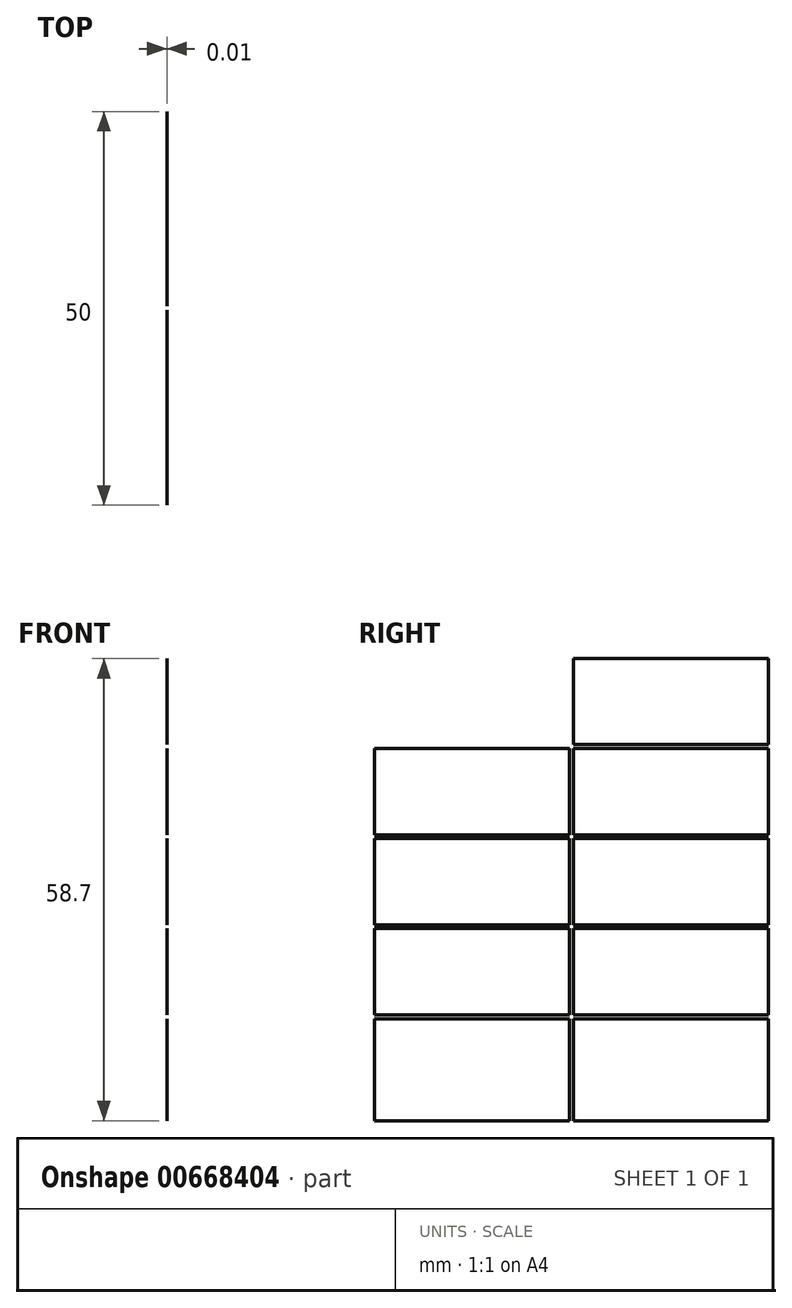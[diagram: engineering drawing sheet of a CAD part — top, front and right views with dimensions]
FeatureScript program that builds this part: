
annotation { "Feature Type Name" : "Feature", "Feature Type Description" : "" }
export const myFeature = defineFeature(function(context is Context, id is Id, definition is map)
    precondition{}
    {
        {
            var Q0;
            Q0=qCreatedBy(makeId("Right.planeOp"),FACE);
            var sketch = newSketch(context, id + "F0", { "sketchPlane" : qUnion([Q0])});
            skPoint(sketch, "E0.0", {"position": v(0, 0) * mm});
            skLineSegment(sketch, "E1.bottom", {"start": v(0, 0) * mm, "end": v(50, 0) * mm});
            skLineSegment(sketch, "E1.top", {"start": v(0, -60) * mm, "end": v(50, -60) * mm});
            skLineSegment(sketch, "E1.left", {"start": v(0, 0) * mm, "end": v(0, -12.24) * mm});
            skLineSegment(sketch, "E1.right", {"start": v(50, 0) * mm, "end": v(50, -12.24) * mm});
            skPoint(sketch, "E2.MirrorP", {"position": v(11.5, 0) * mm});
            skPoint(sketch, "E3.MirrorP", {"position": v(18.5, 0) * mm});
            skPoint(sketch, "E4.MirrorP", {"position": v(30, 0) * mm});
            skLineSegment(sketch, "E5.0", {"start": v(25.25, -60) * mm, "end": v(25.25, -52.76) * mm});
            skLineSegment(sketch, "E6.0", {"start": v(24.75, -60) * mm, "end": v(24.75, -52.76) * mm});
            skLineSegment(sketch, "E7.trimOffspring", {"start": v(25.25, -1.3) * mm, "end": v(50, -1.3) * mm});
            skLineSegment(sketch, "E8.0", {"start": v(0, -12.24) * mm, "end": v(24.75, -12.24) * mm});
            skLineSegment(sketch, "E9.0", {"start": v(0, -12.74) * mm, "end": v(24.75, -12.74) * mm});
            skLineSegment(sketch, "E10.trimOffspring", {"start": v(25.25, -6.52) * mm, "end": v(25.25, -1.3) * mm});
            skLineSegment(sketch, "E11.trimOffspring", {"start": v(25.25, -12.24) * mm, "end": v(50, -12.24) * mm});
            skLineSegment(sketch, "E12.trimOffspring", {"start": v(25.25, -12.24) * mm, "end": v(25.25, -7.02) * mm});
            skLineSegment(sketch, "E13.trimOffspring", {"start": v(25.25, -12.74) * mm, "end": v(50, -12.74) * mm});
            skLineSegment(sketch, "E14.trimOffspring", {"start": v(25.25, -17.95) * mm, "end": v(25.25, -12.74) * mm});
            skLineSegment(sketch, "E15.0", {"start": v(0, -23.67) * mm, "end": v(24.75, -23.67) * mm});
            skLineSegment(sketch, "E16.0", {"start": v(0, -24.17) * mm, "end": v(24.75, -24.17) * mm});
            skLineSegment(sketch, "E17.trimOffspring", {"start": v(25.25, -23.67) * mm, "end": v(50, -23.67) * mm});
            skLineSegment(sketch, "E18.trimOffspring", {"start": v(25.25, -23.67) * mm, "end": v(25.25, -18.45) * mm});
            skLineSegment(sketch, "E19.trimOffspring", {"start": v(25.25, -24.17) * mm, "end": v(50, -24.17) * mm});
            skLineSegment(sketch, "E20.trimOffspring", {"start": v(25.25, -29.39) * mm, "end": v(25.25, -24.17) * mm});
            skLineSegment(sketch, "E21.trimOffspring", {"start": v(24.75, -29.39) * mm, "end": v(24.75, -24.17) * mm});
            skLineSegment(sketch, "E22.0", {"start": v(0, -35.1) * mm, "end": v(24.75, -35.1) * mm});
            skLineSegment(sketch, "E23.0", {"start": v(0, -35.6) * mm, "end": v(24.75, -35.6) * mm});
            skLineSegment(sketch, "E24.trimOffspring", {"start": v(25.25, -35.1) * mm, "end": v(50, -35.1) * mm});
            skLineSegment(sketch, "E25.trimOffspring", {"start": v(25.25, -35.1) * mm, "end": v(25.25, -29.89) * mm});
            skLineSegment(sketch, "E26.trimOffspring", {"start": v(24.75, -35.1) * mm, "end": v(24.75, -29.89) * mm});
            skLineSegment(sketch, "E27.trimOffspring", {"start": v(25.25, -35.6) * mm, "end": v(50, -35.6) * mm});
            skLineSegment(sketch, "E28.trimOffspring", {"start": v(25.25, -40.82) * mm, "end": v(25.25, -35.6) * mm});
            skLineSegment(sketch, "E29.trimOffspring", {"start": v(24.75, -40.82) * mm, "end": v(24.75, -35.6) * mm});
            skLineSegment(sketch, "E30.0", {"start": v(0, -46.54) * mm, "end": v(24.75, -46.54) * mm});
            skLineSegment(sketch, "E31.0", {"start": v(0, -47.04) * mm, "end": v(24.75, -47.04) * mm});
            skLineSegment(sketch, "E32.trimOffspring", {"start": v(25.25, -46.54) * mm, "end": v(50, -46.54) * mm});
            skLineSegment(sketch, "E33.trimOffspring", {"start": v(25.25, -46.54) * mm, "end": v(25.25, -41.32) * mm});
            skLineSegment(sketch, "E34.trimOffspring", {"start": v(24.75, -46.54) * mm, "end": v(24.75, -41.32) * mm});
            skLineSegment(sketch, "E35.trimOffspring", {"start": v(25.25, -47.04) * mm, "end": v(50, -47.04) * mm});
            skLineSegment(sketch, "E36.trimOffspring", {"start": v(25.25, -52.26) * mm, "end": v(25.25, -47.04) * mm});
            skLineSegment(sketch, "E37.trimOffspring", {"start": v(24.75, -52.26) * mm, "end": v(24.75, -47.04) * mm});
            skLineSegment(sketch, "E38", {"start": v(25.25, -6.52) * mm, "end": v(25.25, -7.02) * mm});
            skLineSegment(sketch, "E39", {"start": v(25.25, -17.95) * mm, "end": v(25.25, -18.45) * mm});
            skLineSegment(sketch, "E40", {"start": v(25.25, -29.39) * mm, "end": v(25.25, -29.89) * mm});
            skLineSegment(sketch, "E41", {"start": v(24.75, -29.39) * mm, "end": v(24.75, -29.89) * mm});
            skLineSegment(sketch, "E42", {"start": v(25.25, -40.82) * mm, "end": v(25.25, -41.32) * mm});
            skLineSegment(sketch, "E43", {"start": v(24.75, -40.82) * mm, "end": v(24.75, -41.32) * mm});
            skLineSegment(sketch, "E44", {"start": v(24.75, -52.26) * mm, "end": v(24.75, -52.76) * mm});
            skLineSegment(sketch, "E45", {"start": v(25.25, -52.26) * mm, "end": v(25.25, -52.76) * mm});
            skLineSegment(sketch, "E46.trimOffspring", {"start": v(0, -12.74) * mm, "end": v(0, -23.67) * mm});
            skLineSegment(sketch, "E47.trimOffspring", {"start": v(0, -24.17) * mm, "end": v(0, -35.1) * mm});
            skLineSegment(sketch, "E48.trimOffspring", {"start": v(0, -35.6) * mm, "end": v(0, -46.54) * mm});
            skLineSegment(sketch, "E49.trimOffspring", {"start": v(0, -47.04) * mm, "end": v(0, -60) * mm});
            skLineSegment(sketch, "E50.trimOffspring", {"start": v(50, -47.04) * mm, "end": v(50, -60) * mm});
            skLineSegment(sketch, "E51.trimOffspring", {"start": v(50, -35.6) * mm, "end": v(50, -46.54) * mm});
            skLineSegment(sketch, "E52.trimOffspring", {"start": v(50, -12.74) * mm, "end": v(50, -23.67) * mm});
            skLineSegment(sketch, "E53.trimOffspring", {"start": v(50, -24.17) * mm, "end": v(50, -35.1) * mm});
            skLineSegment(sketch, "E54", {"start": v(12.38, -12.74) * mm, "end": v(12.38, -12.24) * mm});
            skLineSegment(sketch, "E55.0", {"start": v(17.38, -12.74) * mm, "end": v(17.38, -12.24) * mm});
            skLineSegment(sketch, "E56.0", {"start": v(7.38, -12.74) * mm, "end": v(7.38, -12.24) * mm});
            skLineSegment(sketch, "E57", {"start": v(24.75, -12.24) * mm, "end": v(24.75, 0) * mm});
            skLineSegment(sketch, "E58", {"start": v(24.75, -6.12) * mm, "end": v(25.25, -6.12) * mm});
            skLineSegment(sketch, "E59.0", {"start": v(24.75, -9.12) * mm, "end": v(25.25, -9.12) * mm});
            skLineSegment(sketch, "E60.0", {"start": v(24.75, -3.12) * mm, "end": v(25.25, -3.12) * mm});
            skLineSegment(sketch, "E61", {"start": v(24.75, -12.74) * mm, "end": v(24.75, -23.67) * mm});
            skLineSegment(sketch, "E62", {"start": v(24.75, -18.2) * mm, "end": v(25.25, -18.2) * mm});
            skLineSegment(sketch, "E63.0", {"start": v(24.75, -21.2) * mm, "end": v(25.25, -21.2) * mm});
            skLineSegment(sketch, "E64.0", {"start": v(24.75, -15.2) * mm, "end": v(25.25, -15.2) * mm});
            skSolve(sketch);
        }
        {
            var Q0;
            {var subQ1=sQuery(id+"F0.wireOp",EDGE,"6f222dcf-cafe-427f-96f1-de862232ba62.0");Q0=makeQuery(id+"F0.imprint","IMPRINT",FACE,{"disambiguationData":[TD([[makeQuery(id+"F0.imprint","IMPRINT",EDGE,{"derivedFrom":subQ1}),-1.0]])]});}
            var Q1;
            {var subQ1=sQuery(id+"F0.wireOp",EDGE,"E7.trimOffspring");Q1=makeQuery(id+"F0.imprint","IMPRINT",FACE,{"disambiguationData":[TD([[makeQuery(id+"F0.imprint","IMPRINT",EDGE,{"derivedFrom":subQ1}),-1.0]])]});}
            var Q2;
            Q2=makeQuery(id+"F0.imprint","IMPRINT",FACE,{"disambiguationData":[TD([[makeQuery(id+"F0.imprint","IMPRINT",EDGE,{"derivedFrom":sQuery(id+"F0.wireOp",EDGE,"E9.0")}),-1.0]])]});
            var Q3;
            Q3=makeQuery(id+"F0.imprint","IMPRINT",FACE,{"disambiguationData":[TD([[makeQuery(id+"F0.imprint","IMPRINT",EDGE,{"derivedFrom":sQuery(id+"F0.wireOp",EDGE,"E13.trimOffspring")}),-1.0]])]});
            var Q4;
            Q4=makeQuery(id+"F0.imprint","IMPRINT",FACE,{"disambiguationData":[TD([[makeQuery(id+"F0.imprint","IMPRINT",EDGE,{"derivedFrom":sQuery(id+"F0.wireOp",EDGE,"E19.trimOffspring")}),-1.0]])]});
            var Q5;
            Q5=makeQuery(id+"F0.imprint","IMPRINT",FACE,{"disambiguationData":[TD([[makeQuery(id+"F0.imprint","IMPRINT",EDGE,{"derivedFrom":sQuery(id+"F0.wireOp",EDGE,"E16.0")}),-1.0]])]});
            var Q6;
            Q6=makeQuery(id+"F0.imprint","IMPRINT",FACE,{"disambiguationData":[TD([[makeQuery(id+"F0.imprint","IMPRINT",EDGE,{"derivedFrom":sQuery(id+"F0.wireOp",EDGE,"E23.0")}),-1.0]])]});
            var Q7;
            Q7=makeQuery(id+"F0.imprint","IMPRINT",FACE,{"disambiguationData":[TD([[makeQuery(id+"F0.imprint","IMPRINT",EDGE,{"derivedFrom":sQuery(id+"F0.wireOp",EDGE,"E27.trimOffspring")}),-1.0]])]});
            var Q8;
            {var subQ0=sQuery(id+"F0.wireOp",EDGE,"E5.0");Q8=makeQuery(id+"F0.imprint","IMPRINT",FACE,{"disambiguationData":[TD([[makeQuery(id+"F0.imprint","IMPRINT",EDGE,{"derivedFrom":subQ0}),-1.0]])]});}
            var Q9;
            {var subQ0=sQuery(id+"F0.wireOp",EDGE,"E6.0");Q9=makeQuery(id+"F0.imprint","IMPRINT",FACE,{"disambiguationData":[TD([[makeQuery(id+"F0.imprint","IMPRINT",EDGE,{"derivedFrom":subQ0}),1.0]])]});}
            extrude(context, id + "F1", {"entities" : qUnion([Q0, Q1, Q2, Q3, Q4, Q5, Q6, Q7, Q8, Q9]), "depth" : 0.01 * mm, "offsetDistance" : 25 * mm});
        }
    });
